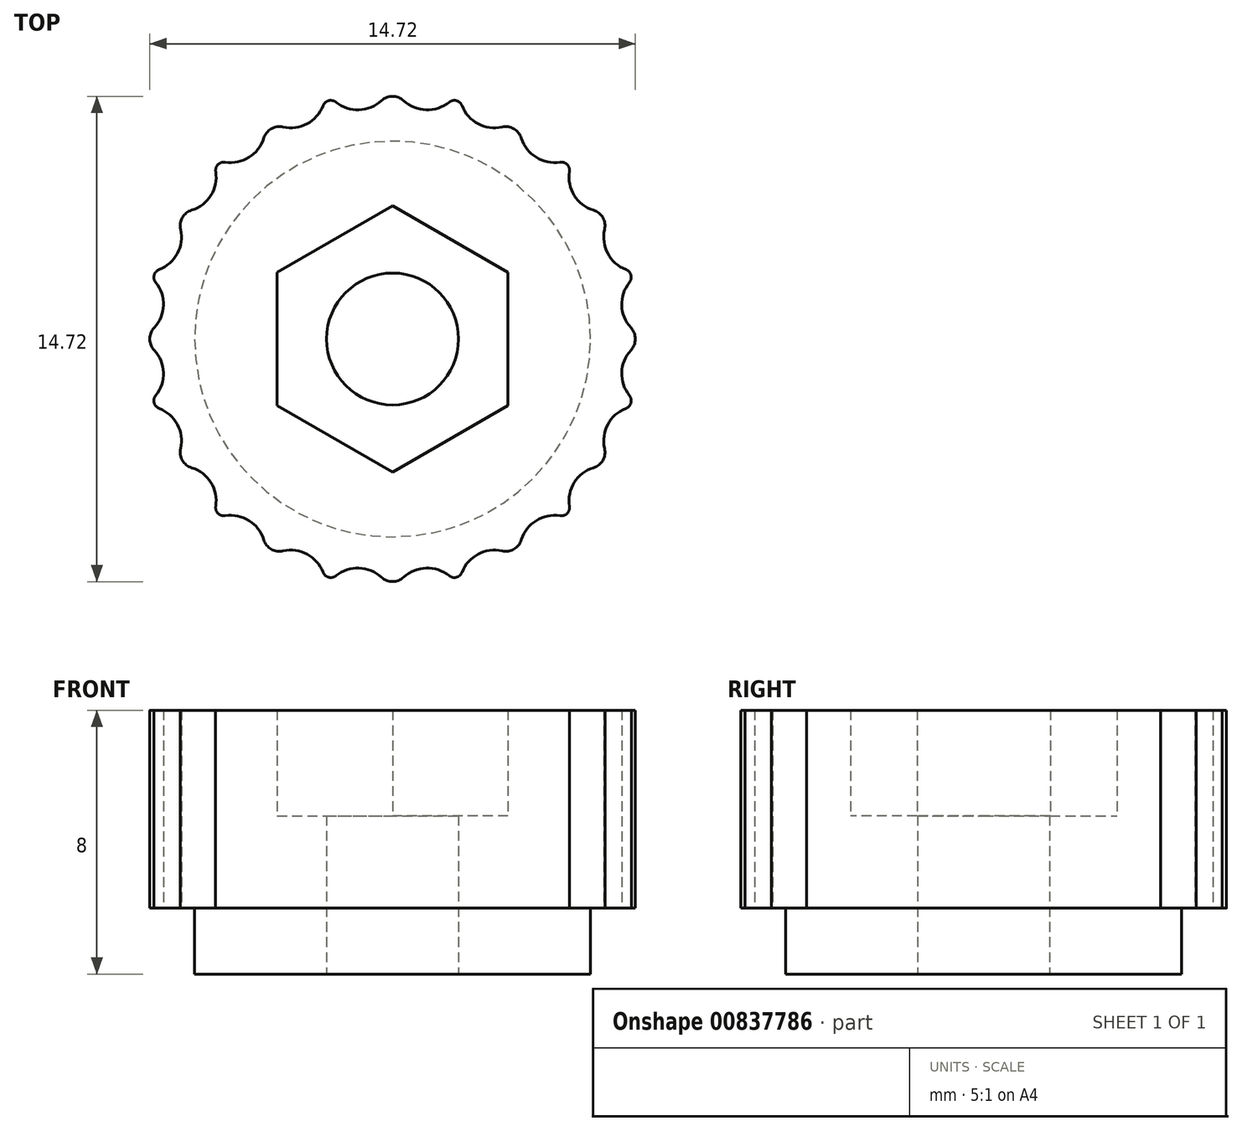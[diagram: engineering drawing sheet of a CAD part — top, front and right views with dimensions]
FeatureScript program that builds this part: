
annotation { "Feature Type Name" : "Feature", "Feature Type Description" : "" }
export const myFeature = defineFeature(function(context is Context, id is Id, definition is map)
    precondition{}
    {
        {
            var Q0;
            Q0=qCreatedBy(makeId("Top.planeOp"),FACE);
            var sketch = newSketch(context, id + "F0", { "sketchPlane" : qUnion([Q0])});
            skLineSegment(sketch, "E0", {"start": v(0, 8) * mm, "end": v(0, 0) * mm});
            skLineSegment(sketch, "E1", {"start": v(0, 0) * mm, "end": v(-8, 0) * mm});
            skLineSegment(sketch, "E2", {"start": v(0, 0) * mm, "end": v(-2.07, 7.73) * mm, "construction": true});
            skLineSegment(sketch, "E3", {"start": v(0, 0) * mm, "end": v(-4, 6.93) * mm, "construction": true});
            skLineSegment(sketch, "E4", {"start": v(0, 0) * mm, "end": v(-5.66, 5.66) * mm, "construction": true});
            skLineSegment(sketch, "E5", {"start": v(0, 0) * mm, "end": v(-6.93, 4) * mm, "construction": true});
            skLineSegment(sketch, "E6", {"start": v(0, 0) * mm, "end": v(-7.73, 2.07) * mm, "construction": true});
            skArc(sketch, "E7", {"start": v(-8, 0) * mm, "mid": v(-6.96, 0.92) * mm, "end": v(-7.73, 2.07) * mm});
            skArc(sketch, "E8", {"start": v(-7.73, 2.07) * mm, "mid": v(-6.48, 2.68) * mm, "end": v(-6.93, 4) * mm});
            skArc(sketch, "E9", {"start": v(-6.93, 4) * mm, "mid": v(-5.57, 4.27) * mm, "end": v(-5.66, 5.66) * mm});
            skArc(sketch, "E10", {"start": v(-5.66, 5.66) * mm, "mid": v(-4.27, 5.57) * mm, "end": v(-4, 6.93) * mm});
            skArc(sketch, "E11", {"start": v(-4, 6.93) * mm, "mid": v(-2.68, 6.48) * mm, "end": v(-2.07, 7.73) * mm});
            skArc(sketch, "E12", {"start": v(-2.07, 7.73) * mm, "mid": v(-0.92, 6.96) * mm, "end": v(0, 8) * mm});
            skLineSegment(sketch, "E13", {"start": v(0, 0) * mm, "end": v(-3.5, 0) * mm, "construction": true});
            skLineSegment(sketch, "E14", {"start": v(0, 0) * mm, "end": v(0, 4.04) * mm, "construction": true});
            skCircle(sketch, "E15", {"center": v(0, 0) * mm, "radius": 4.04 * mm, "construction": true});
            skPoint(sketch, "E16", {"position": v(-3.5, 2.02) * mm});
            skLineSegment(sketch, "E17", {"start": v(-3.5, 2.02) * mm, "end": v(-3.5, 0) * mm});
            skLineSegment(sketch, "E18", {"start": v(-3.5, 2.02) * mm, "end": v(0, 4.04) * mm});
            skArc(sketch, "E19", {"start": v(0, 6) * mm, "mid": v(-4.24, 4.24) * mm, "end": v(-6, 0) * mm});
            skSolve(sketch);
        }
        {
            var Q0;
            {var subQ0=sQuery(id+"F0.wireOp",EDGE,"E7");Q0=makeQuery(id+"F0.imprint","IMPRINT",FACE,{"disambiguationData":[TD([[makeQuery(id+"F0.imprint","IMPRINT",EDGE,{"derivedFrom":subQ0}),-1.0]])]});}
            var Q1;
            {var subQ1=sQuery(id+"F0.wireOp",EDGE,"E17");Q1=makeQuery(id+"F0.imprint","IMPRINT",FACE,{"disambiguationData":[TD([[makeQuery(id+"F0.imprint","IMPRINT",EDGE,{"derivedFrom":subQ1}),-1.0]])]});}
            extrude(context, id + "F1", {"entities" : qUnion([Q0, Q1]), "depth" : 6 * mm, "offsetDistance" : 25 * mm});
        }
        {
            var Q0;
            Q0=makeQuery(id+"F1.opExtrude","SWEPT_EDGE",EDGE,{"disambiguationData":[OSD([sQuery(id+"F0.wireOp",EDGE,"YJfvfTqS-Pjki-TkNm-W0cL-8jKtlRe6EUIt"),sQuery(id+"F0.wireOp",EDGE,"E11"),sQuery(id+"F0.wireOp",EDGE,"E12")])]});
            var Q1;
            Q1=makeQuery(id+"F1.opExtrude","SWEPT_EDGE",EDGE,{"disambiguationData":[OSD([sQuery(id+"F0.wireOp",EDGE,"9fjMVdQh-WNSU-h2hn-eMAG-pHLpN6iex83s"),sQuery(id+"F0.wireOp",EDGE,"E9"),sQuery(id+"F0.wireOp",EDGE,"E10")])]});
            var Q2;
            Q2=makeQuery(id+"F1.opExtrude","SWEPT_EDGE",EDGE,{"disambiguationData":[OSD([sQuery(id+"F0.wireOp",EDGE,"1uZPDy3R-LXX4-vXN9-9vo0-qtQnX8us75y1"),sQuery(id+"F0.wireOp",EDGE,"E7"),sQuery(id+"F0.wireOp",EDGE,"E8")])]});
            fillet(context, id + "F2", {"entities" : qUnion([Q0, Q1, Q2]), "radius" : .25 * mm, "tangentPropagation" : true, "allowEdgeOverflow" : false});
        }
        {
            var Q0;
            Q0=makeQuery(id+"F1.opExtrude","SWEPT_EDGE",EDGE,{"disambiguationData":[OSD([sQuery(id+"F0.wireOp",EDGE,"KobhUoFr-3CUO-Wyh7-YOEs-wexqenTJgbax"),sQuery(id+"F0.wireOp",EDGE,"E10"),sQuery(id+"F0.wireOp",EDGE,"E11")])]});
            var Q1;
            Q1=makeQuery(id+"F1.opExtrude","SWEPT_EDGE",EDGE,{"disambiguationData":[OSD([sQuery(id+"F0.wireOp",EDGE,"0zOxNGcc-i4Hs-fnX7-IKc1-uBtGop8PoNZs"),sQuery(id+"F0.wireOp",EDGE,"E8"),sQuery(id+"F0.wireOp",EDGE,"E9")])]});
            fillet(context, id + "F3", {"entities" : qUnion([Q0, Q1]), "radius" : .5 * mm, "tangentPropagation" : true, "allowEdgeOverflow" : false});
        }
        {
            var Q0;
            {var subQ4=sQuery(id+"F0.wireOp",EDGE,"E17");Q0=makeQuery(id+"F0.imprint","IMPRINT",FACE,{"disambiguationData":[TD([[makeQuery(id+"F0.imprint","IMPRINT",EDGE,{"derivedFrom":subQ4}),1.0]])]});}
            extrude(context, id + "F4", {"entities" : qUnion([Q0]), "operationType" : NewBodyOperationType.ADD, "depth" : 2.8 * mm, "offsetDistance" : 25 * mm});
        }
        {
            var Q0;
            {var subQ1=sQuery(id+"F0.wireOp",EDGE,"E17");Q0=makeQuery(id+"F0.imprint","IMPRINT",FACE,{"disambiguationData":[TD([[makeQuery(id+"F0.imprint","IMPRINT",EDGE,{"derivedFrom":subQ1}),-1.0]])]});}
            var Q1;
            {var subQ4=sQuery(id+"F0.wireOp",EDGE,"E17");Q1=makeQuery(id+"F0.imprint","IMPRINT",FACE,{"disambiguationData":[TD([[makeQuery(id+"F0.imprint","IMPRINT",EDGE,{"derivedFrom":subQ4}),1.0]])]});}
            extrude(context, id + "F5", {"entities" : qUnion([Q0, Q1]), "operationType" : NewBodyOperationType.ADD, "oppositeDirection" : true, "depth" : 2 * mm, "offsetDistance" : 25 * mm});
        }
        {
            var Q0;
            Q0=makeQuery(id+"F1.opExtrude","SWEPT_BODY",BODY,{"disambiguationData":[OSD([sQuery(id+"F0.wireOp",EDGE,"E0"),sQuery(id+"F0.wireOp",EDGE,"E1"),sQuery(id+"F0.wireOp",EDGE,"E7"),sQuery(id+"F0.wireOp",EDGE,"E8"),sQuery(id+"F0.wireOp",EDGE,"E9"),sQuery(id+"F0.wireOp",EDGE,"E10"),sQuery(id+"F0.wireOp",EDGE,"E11"),sQuery(id+"F0.wireOp",EDGE,"E12"),sQuery(id+"F0.wireOp",EDGE,"E17"),sQuery(id+"F0.wireOp",EDGE,"E18")])]});
            var Q1;
            {var subQ0=sQuery(id+"F0.wireOp",EDGE,"E1");Q1=makeQuery(id+"F5.boolean.opBoolean","MERGE",FACE,{"derivedFrom":[makeQuery(id+"F4.boolean.opBoolean","MERGE",FACE,{"derivedFrom":[makeQuery(id+"F1.opExtrude","SWEPT_FACE",FACE,{"disambiguationData":[OSD([subQ0])]}),makeQuery(id+"F4.opExtrude","SWEPT_FACE",FACE,{"disambiguationData":[OSD([subQ0])]})]}),makeQuery(id+"F5.opExtrude","SWEPT_FACE",FACE,{"disambiguationData":[OSD([subQ0])]})]});}
            mirror(context, id + "F6", {"operationType" : NewBodyOperationType.ADD, "entities" : qUnion([Q0]), "mirrorPlane" : qUnion([Q1])});
        }
        {
            var Q0;
            Q0=makeQuery(id+"F1.opExtrude","SWEPT_BODY",BODY,{"disambiguationData":[OSD([sQuery(id+"F0.wireOp",EDGE,"E0"),sQuery(id+"F0.wireOp",EDGE,"E1"),sQuery(id+"F0.wireOp",EDGE,"E7"),sQuery(id+"F0.wireOp",EDGE,"E8"),sQuery(id+"F0.wireOp",EDGE,"E9"),sQuery(id+"F0.wireOp",EDGE,"E10"),sQuery(id+"F0.wireOp",EDGE,"E11"),sQuery(id+"F0.wireOp",EDGE,"E12"),sQuery(id+"F0.wireOp",EDGE,"E17"),sQuery(id+"F0.wireOp",EDGE,"E18")])]});
            var Q1;
            {var subQ0=sQuery(id+"F0.wireOp",EDGE,"E0");var subQ1=makeQuery(id+"F5.boolean.opBoolean","MERGE",FACE,{"derivedFrom":[makeQuery(id+"F4.boolean.opBoolean","MERGE",FACE,{"derivedFrom":[makeQuery(id+"F1.opExtrude","SWEPT_FACE",FACE,{"disambiguationData":[OSD([subQ0])]}),makeQuery(id+"F4.opExtrude","SWEPT_FACE",FACE,{"disambiguationData":[OSD([subQ0])]})]}),makeQuery(id+"F5.opExtrude","SWEPT_FACE",FACE,{"disambiguationData":[OSD([subQ0])]})]});Q1=makeQuery(id+"F6.boolean.opBoolean","MERGE",FACE,{"derivedFrom":[subQ1,makeQuery(id+"F6.opPattern","COPY",FACE,{"derivedFrom":subQ1,"instanceName":"1"})]});}
            mirror(context, id + "F7", {"operationType" : NewBodyOperationType.ADD, "entities" : qUnion([Q0]), "mirrorPlane" : qUnion([Q1])});
        }
        {
            var Q0;
            {var subQ0=makeQuery(id+"F6.opPattern","COPY",EDGE,{"derivedFrom":makeQuery(id+"F1.opExtrude","SWEPT_EDGE",EDGE,{"disambiguationData":[OSD([sQuery(id+"F0.wireOp",EDGE,"E0"),sQuery(id+"F0.wireOp",EDGE,"E12")])]}),"instanceName":"1"});Q0=makeQuery(id+"F7.boolean.opBoolean","MERGE",EDGE,{"derivedFrom":[subQ0,makeQuery(id+"F7.opPattern","COPY",EDGE,{"derivedFrom":subQ0,"instanceName":"1"})]});}
            var Q1;
            {var subQ0=makeQuery(id+"F1.opExtrude","SWEPT_EDGE",EDGE,{"disambiguationData":[OSD([sQuery(id+"F0.wireOp",EDGE,"E1"),sQuery(id+"F0.wireOp",EDGE,"E7")])]});Q1=makeQuery(id+"F7.opPattern","COPY",EDGE,{"derivedFrom":makeQuery(id+"F6.boolean.opBoolean","MERGE",EDGE,{"derivedFrom":[subQ0,makeQuery(id+"F6.opPattern","COPY",EDGE,{"derivedFrom":subQ0,"instanceName":"1"})]}),"instanceName":"1"});}
            var Q2;
            {var subQ0=makeQuery(id+"F1.opExtrude","SWEPT_EDGE",EDGE,{"disambiguationData":[OSD([sQuery(id+"F0.wireOp",EDGE,"E0"),sQuery(id+"F0.wireOp",EDGE,"E12")])]});Q2=makeQuery(id+"F7.boolean.opBoolean","MERGE",EDGE,{"derivedFrom":[subQ0,makeQuery(id+"F7.opPattern","COPY",EDGE,{"derivedFrom":subQ0,"instanceName":"1"})]});}
            var Q3;
            {var subQ0=makeQuery(id+"F1.opExtrude","SWEPT_EDGE",EDGE,{"disambiguationData":[OSD([sQuery(id+"F0.wireOp",EDGE,"E1"),sQuery(id+"F0.wireOp",EDGE,"E7")])]});Q3=makeQuery(id+"F6.boolean.opBoolean","MERGE",EDGE,{"derivedFrom":[subQ0,makeQuery(id+"F6.opPattern","COPY",EDGE,{"derivedFrom":subQ0,"instanceName":"1"})]});}
            fillet(context, id + "F8", {"entities" : qUnion([Q0, Q1, Q2, Q3]), "radius" : .5 * mm, "tangentPropagation" : true, "allowEdgeOverflow" : false});
        }
        {
            var Q0;
            {var subQ0=makeQuery(id+"F5.opExtrude","CAP_FACE",FACE,{"disambiguationData":[OSD([sQuery(id+"F0.wireOp",EDGE,"E0"),sQuery(id+"F0.wireOp",EDGE,"E1"),sQuery(id+"F0.wireOp",EDGE,"E19")])],"isStart":false});var subQ1=makeQuery(id+"F6.boolean.opBoolean","MERGE",FACE,{"derivedFrom":[subQ0,makeQuery(id+"F6.opPattern","COPY",FACE,{"derivedFrom":subQ0,"instanceName":"1"})]});Q0=makeQuery(id+"F7.boolean.opBoolean","MERGE",FACE,{"derivedFrom":[subQ1,makeQuery(id+"F7.opPattern","COPY",FACE,{"derivedFrom":subQ1,"instanceName":"1"})]});}
            var sketch = newSketch(context, id + "F9", { "sketchPlane" : qUnion([Q0])});
            skCircle(sketch, "E20", {"center": v(0, 0) * mm, "radius": 2 * mm});
            skSolve(sketch);
        }
        {
            var Q0;
            Q0 = qSketchRegion(id + "F9", true);
            extrude(context, id + "F10", {"entities" : qUnion([Q0]), "operationType" : NewBodyOperationType.REMOVE, "oppositeDirection" : true, "depth" : 4.8 * mm, "offsetDistance" : 25 * mm});
        }
    });
